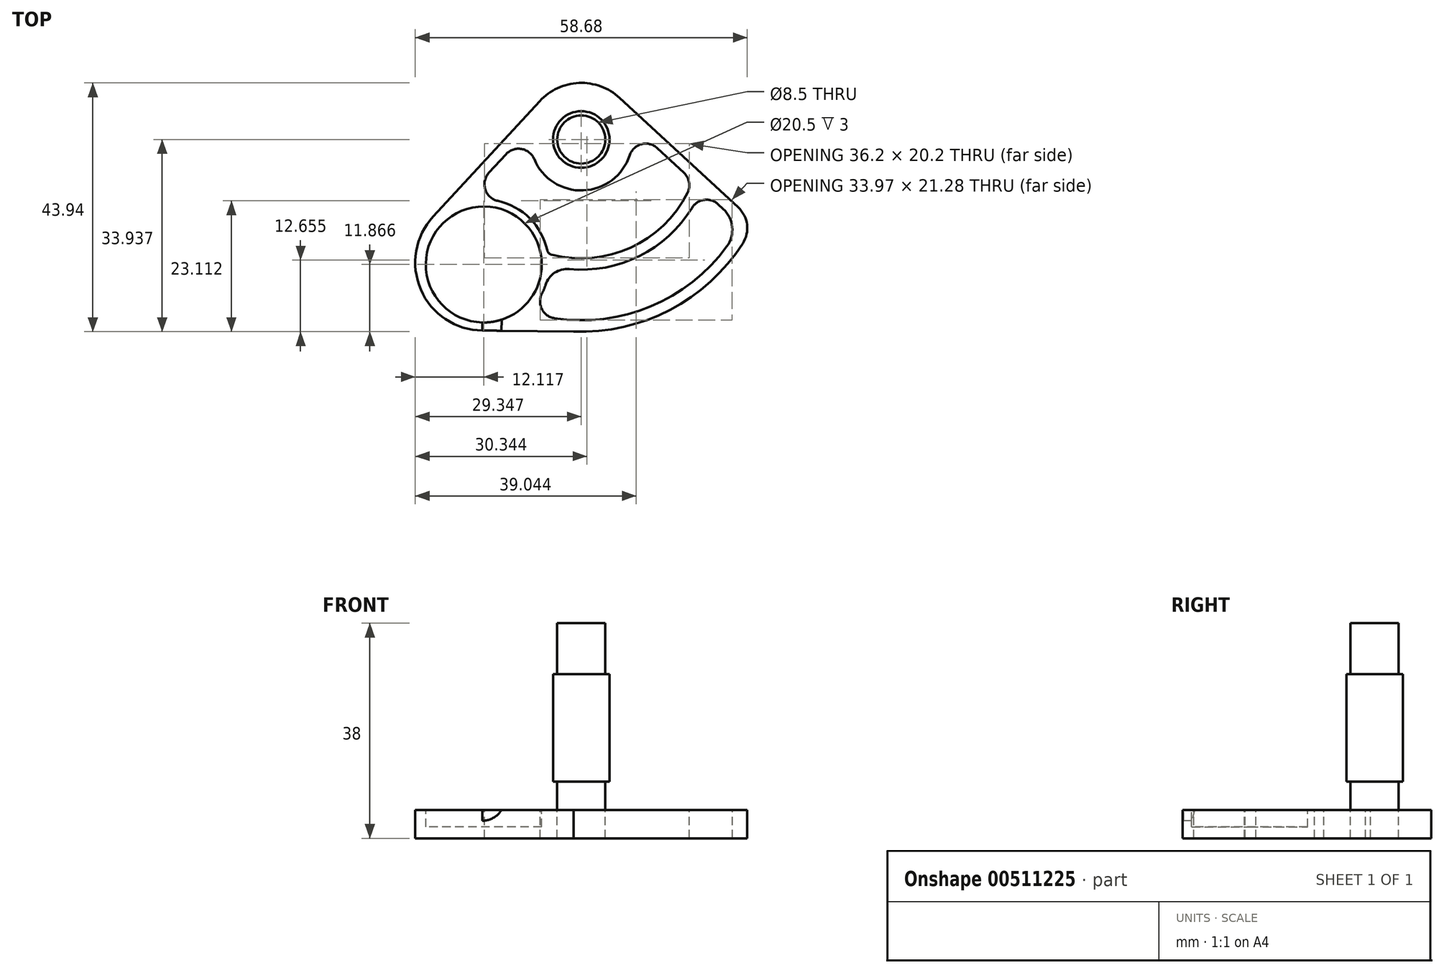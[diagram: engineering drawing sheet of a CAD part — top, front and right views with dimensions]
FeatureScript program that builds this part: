
annotation { "Feature Type Name" : "Feature", "Feature Type Description" : "" }
export const myFeature = defineFeature(function(context is Context, id is Id, definition is map)
    precondition{}
    {
        {
            var Q0;
            Q0=qCreatedBy(makeId("Top.planeOp"),FACE);
            var sketch = newSketch(context, id + "F0", { "sketchPlane" : qUnion([Q0])});
            skCircle(sketch, "E0", {"center": v(31.1, -55.05) * mm, "radius": 5 * mm});
            skCircle(sketch, "E1", {"center": v(31.1, -55.05) * mm, "radius": 4.25 * mm});
            skCircle(sketch, "E2", {"center": v(13.88, -77.12) * mm, "radius": 10.25 * mm});
            skPoint(sketch, "E3", {"position": v(54.93, -69.76) * mm});
            skLineSegment(sketch, "E4", {"start": v(23.76, -48.27) * mm, "end": v(4.95, -68.66) * mm});
            skLineSegment(sketch, "E5", {"start": v(37.89, -47.7) * mm, "end": v(58.84, -67.04) * mm});
            skLineSegment(sketch, "E6", {"start": v(29.74, -88.96) * mm, "end": v(13.64, -88.8) * mm});
            skArc(sketch, "E7.filletArc", {"start": v(4.95, -68.66) * mm, "mid": v(2.75, -81.55) * mm, "end": v(13.64, -88.8) * mm});
            skPoint(sketch, "E8.visualSharp", {"position": v(30.54, -40.92) * mm});
            skArc(sketch, "E8.filletArc", {"start": v(37.89, -47.7) * mm, "mid": v(30.7, -45.06) * mm, "end": v(23.76, -48.27) * mm});
            skArc(sketch, "E9", {"start": v(22.8, -58.52) * mm, "mid": v(31.47, -64.05) * mm, "end": v(39.66, -57.85) * mm});
            skArc(sketch, "E10", {"start": v(24.14, -82.3) * mm, "mid": v(24.5, -81.51) * mm, "end": v(24.8, -80.7) * mm});
            skLineSegment(sketch, "E11", {"start": v(14.8, -60.93) * mm, "end": v(17.83, -57.64) * mm});
            skLineSegment(sketch, "E12", {"start": v(44.55, -56.57) * mm, "end": v(49.24, -60.9) * mm});
            skPoint(sketch, "E13.endSnap0", {"position": v(14.35, -58.46) * mm});
            skPoint(sketch, "E14.orphan", {"position": v(57.46, -58.46) * mm});
            skArc(sketch, "E15", {"start": v(25.83, -75.38) * mm, "mid": v(39.8, -74.17) * mm, "end": v(49.89, -64.45) * mm});
            skArc(sketch, "E16", {"start": v(28.98, -77.95) * mm, "mid": v(41.38, -75.63) * mm, "end": v(50.7, -67.11) * mm});
            skArc(sketch, "E17", {"start": v(26.38, -86.63) * mm, "mid": v(43.37, -84.53) * mm, "end": v(56.84, -73.96) * mm});
            skArc(sketch, "E18", {"start": v(29.74, -88.96) * mm, "mid": v(46.76, -85.17) * mm, "end": v(59.65, -73.41) * mm});
            skLineSegment(sketch, "E19.trimOffspring", {"start": v(55.28, -66.48) * mm, "end": v(56.2, -67.32) * mm});
            skPoint(sketch, "E20.visualSharp", {"position": v(59.25, -70.14) * mm});
            skArc(sketch, "E20.filletArc", {"start": v(56.84, -73.96) * mm, "mid": v(57.78, -70.52) * mm, "end": v(56.2, -67.32) * mm});
            skArc(sketch, "E21.filletArc", {"start": v(59.65, -73.41) * mm, "mid": v(60.4, -70.08) * mm, "end": v(58.84, -67.04) * mm});
            skArc(sketch, "E22.trimOffspring", {"start": v(25.1, -74.63) * mm, "mid": v(22, -68.99) * mm, "end": v(16.36, -65.9) * mm});
            skPoint(sketch, "E23.visualSharp", {"position": v(21.7, -85.56) * mm});
            skArc(sketch, "E23.filletArc", {"start": v(24.14, -82.3) * mm, "mid": v(24.16, -85.04) * mm, "end": v(26.38, -86.63) * mm});
            skPoint(sketch, "E24.visualSharp", {"position": v(25.37, -77.33) * mm});
            skArc(sketch, "E24.filletArc", {"start": v(28.98, -77.95) * mm, "mid": v(26.41, -78.6) * mm, "end": v(24.8, -80.7) * mm});
            skPoint(sketch, "E25.visualSharp", {"position": v(25.22, -75.21) * mm});
            skArc(sketch, "E25.filletArc", {"start": v(25.1, -74.63) * mm, "mid": v(25.36, -75.1) * mm, "end": v(25.83, -75.38) * mm});
            skPoint(sketch, "E26.visualSharp", {"position": v(9.76, -66.39) * mm});
            skArc(sketch, "E26.filletArc", {"start": v(14.8, -60.93) * mm, "mid": v(14.14, -63.86) * mm, "end": v(16.36, -65.9) * mm});
            skPoint(sketch, "E27.visualSharp", {"position": v(22.43, -52.66) * mm});
            skArc(sketch, "E27.filletArc", {"start": v(22.8, -58.52) * mm, "mid": v(20.56, -56.72) * mm, "end": v(17.83, -57.64) * mm});
            skPoint(sketch, "E28.visualSharp", {"position": v(39.56, -51.97) * mm});
            skArc(sketch, "E28.filletArc", {"start": v(44.55, -56.57) * mm, "mid": v(41.76, -55.87) * mm, "end": v(39.66, -57.85) * mm});
            skPoint(sketch, "E29.visualSharp", {"position": v(50.8, -62.34) * mm});
            skArc(sketch, "E29.filletArc", {"start": v(49.89, -64.45) * mm, "mid": v(50.16, -62.57) * mm, "end": v(49.24, -60.9) * mm});
            skPoint(sketch, "E30.visualSharp", {"position": v(52.38, -63.8) * mm});
            skArc(sketch, "E30.filletArc", {"start": v(55.28, -66.48) * mm, "mid": v(52.84, -65.71) * mm, "end": v(50.7, -67.11) * mm});
            skSolve(sketch);
        }
        {
            var Q0;
            Q0=makeQuery(id+"F0.imprint","IMPRINT",FACE,{"disambiguationData":[TD([[makeQuery(id+"F0.imprint","IMPRINT",EDGE,{"derivedFrom":sQuery(id+"F0.wireOp",EDGE,"ScRWYDua-mYab-p1bD-zXnp-wvtpqM8LOkLs.bottom")}),-1.0]])]});
            var Q1;
            Q1=makeQuery(id+"F0.imprint","IMPRINT",FACE,{"disambiguationData":[TD([[makeQuery(id+"F0.imprint","IMPRINT",EDGE,{"derivedFrom":sQuery(id+"F0.wireOp",EDGE,"E2")}),1.0]])]});
            var Q2;
            Q2=makeQuery(id+"F0.imprint","IMPRINT",FACE,{"disambiguationData":[TD([[makeQuery(id+"F0.imprint","IMPRINT",EDGE,{"derivedFrom":sQuery(id+"F0.wireOp",EDGE,"W70nhKsN-JiaP-Kaip-Gnzn-Tj85YjjBPHD4.bottom")}),1.0]])]});
            var Q3;
            Q3=makeQuery(id+"F0.imprint","IMPRINT",FACE,{"disambiguationData":[TD([[makeQuery(id+"F0.imprint","IMPRINT",EDGE,{"derivedFrom":sQuery(id+"F0.wireOp",EDGE,"ScRWYDua-mYab-p1bD-zXnp-wvtpqM8LOkLs.top")}),1.0]])]});
            var Q4;
            Q4=makeQuery(id+"F0.imprint","IMPRINT",FACE,{"disambiguationData":[TD([[makeQuery(id+"F0.imprint","IMPRINT",EDGE,{"derivedFrom":sQuery(id+"F0.wireOp",EDGE,"E0")}),-1.0]])]});
            var Q5;
            {var subQ0=sQuery(id+"F0.wireOp",EDGE,"yKBMlOZL-a8V5-8eGt-BoQL-3bW9PtVKJtAu");Q5=makeQuery(id+"F0.imprint","IMPRINT",FACE,{"disambiguationData":[TD([[makeQuery(id+"F0.imprint","IMPRINT",EDGE,{"derivedFrom":subQ0}),1.0]])]});}
            var Q6;
            {var subQ0=sQuery(id+"F0.wireOp",EDGE,"GyASaPuT-2NCA-YP9n-uqU3-XCFCOTF9hxUf");Q6=makeQuery(id+"F0.imprint","IMPRINT",FACE,{"disambiguationData":[TD([[makeQuery(id+"F0.imprint","IMPRINT",EDGE,{"derivedFrom":subQ0}),-1.0]])]});}
            var Q7;
            {var subQ0=sQuery(id+"F0.wireOp",EDGE,"thUjPLeQ-msCZ-fr84-VyUT-lr2uj8MLr4R7");Q7=makeQuery(id+"F0.imprint","IMPRINT",FACE,{"disambiguationData":[TD([[makeQuery(id+"F0.imprint","IMPRINT",EDGE,{"derivedFrom":subQ0}),-1.0]])]});}
            var Q8;
            Q8=makeQuery(id+"F0.imprint","IMPRINT",FACE,{"disambiguationData":[TD([[makeQuery(id+"F0.imprint","IMPRINT",EDGE,{"derivedFrom":sQuery(id+"F0.wireOp",EDGE,"E0")}),1.0]])]});
            var Q9;
            {var subQ0=sQuery(id+"F0.wireOp",EDGE,"E15");Q9=makeQuery(id+"F0.imprint","IMPRINT",FACE,{"disambiguationData":[TD([[makeQuery(id+"F0.imprint","IMPRINT",EDGE,{"derivedFrom":subQ0}),-1.0]])]});}
            var Q10;
            {var subQ0=sQuery(id+"F0.wireOp",EDGE,"E17");Q10=makeQuery(id+"F0.imprint","IMPRINT",FACE,{"disambiguationData":[TD([[makeQuery(id+"F0.imprint","IMPRINT",EDGE,{"derivedFrom":subQ0}),-1.0]])]});}
            extrude(context, id + "F1", {"entities" : qUnion([Q0, Q1, Q2, Q3, Q4, Q5, Q6, Q7, Q8, Q9, Q10]), "oppositeDirection" : true, "depth" : 5 * mm, "offsetDistance" : 25 * mm});
        }
        {
            var Q0;
            Q0=makeQuery(id+"F0.imprint","IMPRINT",FACE,{"disambiguationData":[TD([[makeQuery(id+"F0.imprint","IMPRINT",EDGE,{"derivedFrom":sQuery(id+"F0.wireOp",EDGE,"E1")}),1.0]])]});
            extrude(context, id + "F2", {"entities" : qUnion([Q0]), "depth" : 33 * mm, "offsetDistance" : 25 * mm});
        }
        {
            var Q0;
            Q0=makeQuery(id+"F0.imprint","IMPRINT",FACE,{"disambiguationData":[TD([[makeQuery(id+"F0.imprint","IMPRINT",EDGE,{"derivedFrom":sQuery(id+"F0.wireOp",EDGE,"E0")}),1.0]])]});
            extrude(context, id + "F3", {"entities" : qUnion([Q0]), "operationType" : NewBodyOperationType.ADD, "depth" : 24 * mm, "offsetDistance" : 25 * mm});
        }
        {
            var Q0;
            Q0=makeQuery(id+"F0.imprint","IMPRINT",FACE,{"disambiguationData":[TD([[makeQuery(id+"F0.imprint","IMPRINT",EDGE,{"derivedFrom":sQuery(id+"F0.wireOp",EDGE,"E2")}),1.0]])]});
            extrude(context, id + "F4", {"entities" : qUnion([Q0]), "operationType" : NewBodyOperationType.REMOVE, "oppositeDirection" : true, "depth" : 3 * mm});
        }
        {
            var Q0;
            Q0=makeQuery(id+"F0.imprint","IMPRINT",FACE,{"disambiguationData":[TD([[makeQuery(id+"F0.imprint","IMPRINT",EDGE,{"derivedFrom":sQuery(id+"F0.wireOp",EDGE,"E0")}),1.0]])]});
            extrude(context, id + "F5", {"entities" : qUnion([Q0]), "operationType" : NewBodyOperationType.REMOVE, "depth" : 5 * mm, "offsetDistance" : 25 * mm});
        }
        {
            var Q0;
            Q0=makeQuery(id+"F1.opExtrude","SWEPT_FACE",FACE,{"disambiguationData":[OSD([sQuery(id+"F0.wireOp",EDGE,"E6")])]});
            var sketch = newSketch(context, id + "F6", { "sketchPlane" : qUnion([Q0])});
            skLineSegment(sketch, "E31.0", {"start": v(30.67, 0) * mm, "end": v(14.58, 0) * mm});
            skLineSegment(sketch, "E31.1", {"start": v(14.58, -5) * mm, "end": v(14.58, 0) * mm});
            skArc(sketch, "E32", {"start": v(14.58, -1.9) * mm, "mid": v(16.5, -1.38) * mm, "end": v(17.94, 0) * mm});
            skArc(sketch, "E33.MirrorCS", {"start": v(14.58, -1.9) * mm, "mid": v(12.65, -1.38) * mm, "end": v(11.21, 0) * mm});
            skLineSegment(sketch, "E34", {"start": v(11.21, 0) * mm, "end": v(17.94, 0) * mm});
            skSolve(sketch);
        }
        {
            var Q0;
            {var subQ3=sQuery(id+"F6.wireOp",EDGE,"E33.MirrorCS");Q0=makeQuery(id+"F6.imprint","IMPRINT",FACE,{"disambiguationData":[TD([[makeQuery(id+"F6.imprint","IMPRINT",EDGE,{"derivedFrom":subQ3}),-1.0]])]});}
            var Q1;
            {var subQ3=sQuery(id+"F6.wireOp",EDGE,"E32");Q1=makeQuery(id+"F6.imprint","IMPRINT",FACE,{"disambiguationData":[TD([[makeQuery(id+"F6.imprint","IMPRINT",EDGE,{"derivedFrom":subQ3}),1.0]])]});}
            extrude(context, id + "F7", {"entities" : qUnion([Q0, Q1]), "operationType" : NewBodyOperationType.REMOVE, "endBound" : BoundingType.UP_TO_NEXT, "oppositeDirection" : true, "depth" : 25 * mm, "offsetDistance" : 25 * mm});
        }
    });
